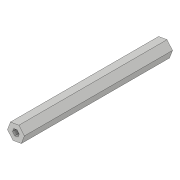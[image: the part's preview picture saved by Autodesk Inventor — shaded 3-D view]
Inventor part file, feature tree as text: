
AUTODESK INVENTOR PART (.ipt)
format: ipt  version: 2018 (Build 220112000, 112)  size: 83,456 bytes
history: native  units: in
note: dims shown in document units (in); Inventor stores cm internally (conversion verified against a paired STEP export)
features: extrude x1, sketch x1
ambient origin geometry x8: Origin, YZ Plane, XZ Plane, XY Plane, X Axis, Y Axis, Z Axis, Center Point
bodies: Solid1 (feature_tree)
feature tree (2):
  extrude  "Extrusion1"  Depth=0.1969in
  sketch  "Sketch1"  dims[d0=0.5in d1=0.1969in d2=5.0in d3=0.0in]
